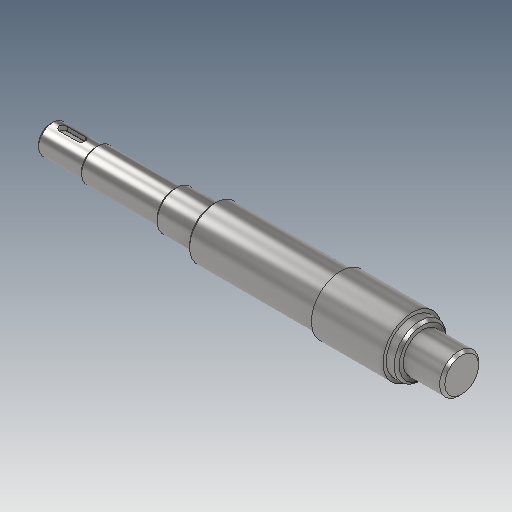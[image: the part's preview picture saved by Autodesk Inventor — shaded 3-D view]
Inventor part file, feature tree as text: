
AUTODESK INVENTOR PART (.ipt)
format: ipt  version: 2025 (Build 290162000, 162)  size: 207,872 bytes
history: native  units: mm
features: chamfer x6, other x5, revolve x1
ambient origin geometry x6: Origin, XZ Plane, XY Plane, X Axis, Y Axis, Z Axis
bodies: 实体1 (feature_tree)
feature tree (12):
  other  "{BB8FE430-83BF-418D-8DF9-9B323D3DB9B9}"
  revolve  "旋转1"  [1 undecoded]
  chamfer  "倒角1"  Distance=22.0mm
  chamfer  "倒角2"  Distance=25.0mm
  chamfer  "倒角3"  Distance=30.0mm
  chamfer  "倒角4"  Distance=40.0mm
  chamfer  "倒角5"  Distance=45.0mm
  chamfer  "倒角6"  Distance=40.0mm
  other  "键槽1"
  other  "起始平面"
  other  "主草图"
  other  "轴键槽"
note: 1 required parameter value undecoded (feature->parameter linkage not recoverable at this tier; creation-order binding heuristic only, values carry confidence <= 0.55)
